# Revit family: PLANK_AVUS_LOUNGE_CHAIR
name_source: partatom
category: Arredi
units: mm (PartAtom-declared; Revit-internal decimal feet)

## family parameters
Condiviso = No
Host = Superficie
Punto di calcolo locali = No
Taglio con vuoti quando caricato = No

## types (2) — shared parameters
AVAILABLE FINISHES = Natural leather available in different colours
BADGE = https://bim.archiproducts.com
COLLECTION = Avus
DEPTH = 730 mm
Descrizione = Upholstered lounge chair
HEIGHT = 820 mm
MATERIAL DESCRIPTION = Lounge chair, base and seat shell in plastic, upholstery in polyurethane foam (flame retardant), covering in natural leather.
Modello = AVUS
PRODUCT CODE = 1920-12
PRODUCT SHEET = https://www.archiproducts.com
Produttore = PLANK
Prospetto di default = 1219 mm
SEAT HEIGHT = 430 mm
TECHNICAL SHEET = https://www.plank.it
URL = https://www.plank.it
WIDTH = 730 mm

## per-type parameters (varying)
| type | BODY MATERIAL | STRUCTURE MATERIAL |
| ABS BLACK MATT - DANI LEATHER FLORIDA 2020 | DANI_LEATHER_FLORIDA_2020 | PLANK_BLACK_MATT |
| ABS PEARL MOUSE GRAY MATT - DANI LEATHER FLORIDA 2020 | DANI_LEATHER_FLORIDA_2062 | PLANK_PEARL_MOUSE_GRAY_MATT |
